# Revit family: Edo exist_window dbl-hung 2-unit
name_source: partatom
category: Windows
revit_build: Autodesk Revit Architecture 2012 (Build: 20110916_2132(x64)
units: mm (PartAtom-declared; Revit-internal decimal feet)

## types (1)
- exist 5-6 x 5-6
    Assembly Code = B2020100
    Description = x
    Height = 5' - 7 1/2"
    Keynote = 08500.WD
    Manufacturer = x
    Model = x
    Wall Closure = By host
    Width = 5' - 7 1/2"
    default sash height yN = Yes
    ext cap trim yN = No
    ext face offset = 4"
    frame exterior = 08550 windows- existing
    frame interior = 08100 interior trim- white
    glass = Glass
    grill width = 3/4"
    grille lower yN = Yes
    grille spaces_horiz = 2
    grille spaces_vert lower = 3
    grille spaces_vert upper = 3
    grille upper yN = Yes
    shutter color = 08550 window shutter solid- existing
    shutter face offset = 1"
    shutter side offset = 3"
    shutterW = 1' - 7"
    trim depth- exterior = 2"
    trim exterior = 08550 windows- existing
    trim interior = 08100 interior trim- white
    trim width- exterior = 4"
    trim width- interior = 4"
    upper sash height = 2' - 0"

## geometry (parser evidence)
native form markers: Sweep x9
no freeform markers — native parametric forms only
